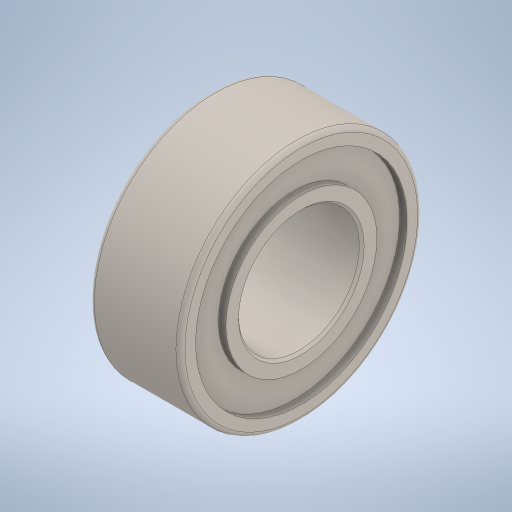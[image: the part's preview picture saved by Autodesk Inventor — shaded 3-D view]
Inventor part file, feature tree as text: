
AUTODESK INVENTOR PART (.ipt)
format: ipt  version: 2024 (Build 280153000, 153)  size: 316,416 bytes
history: native  units: in
note: dims shown in document units (in); Inventor stores cm internally (conversion verified against a paired STEP export)
features: chamfer x1
ambient origin geometry x8: Origin, YZ Plane, XZ Plane, XY Plane, X Axis, Y Axis, Z Axis, Center Point
bodies: Solid1 (feature_tree)
feature tree (1):
  chamfer  "Chamfer1"  [1 undecoded]
note: 1 required parameter value undecoded (feature->parameter linkage not recoverable at this tier; creation-order binding heuristic only, values carry confidence <= 0.55)
